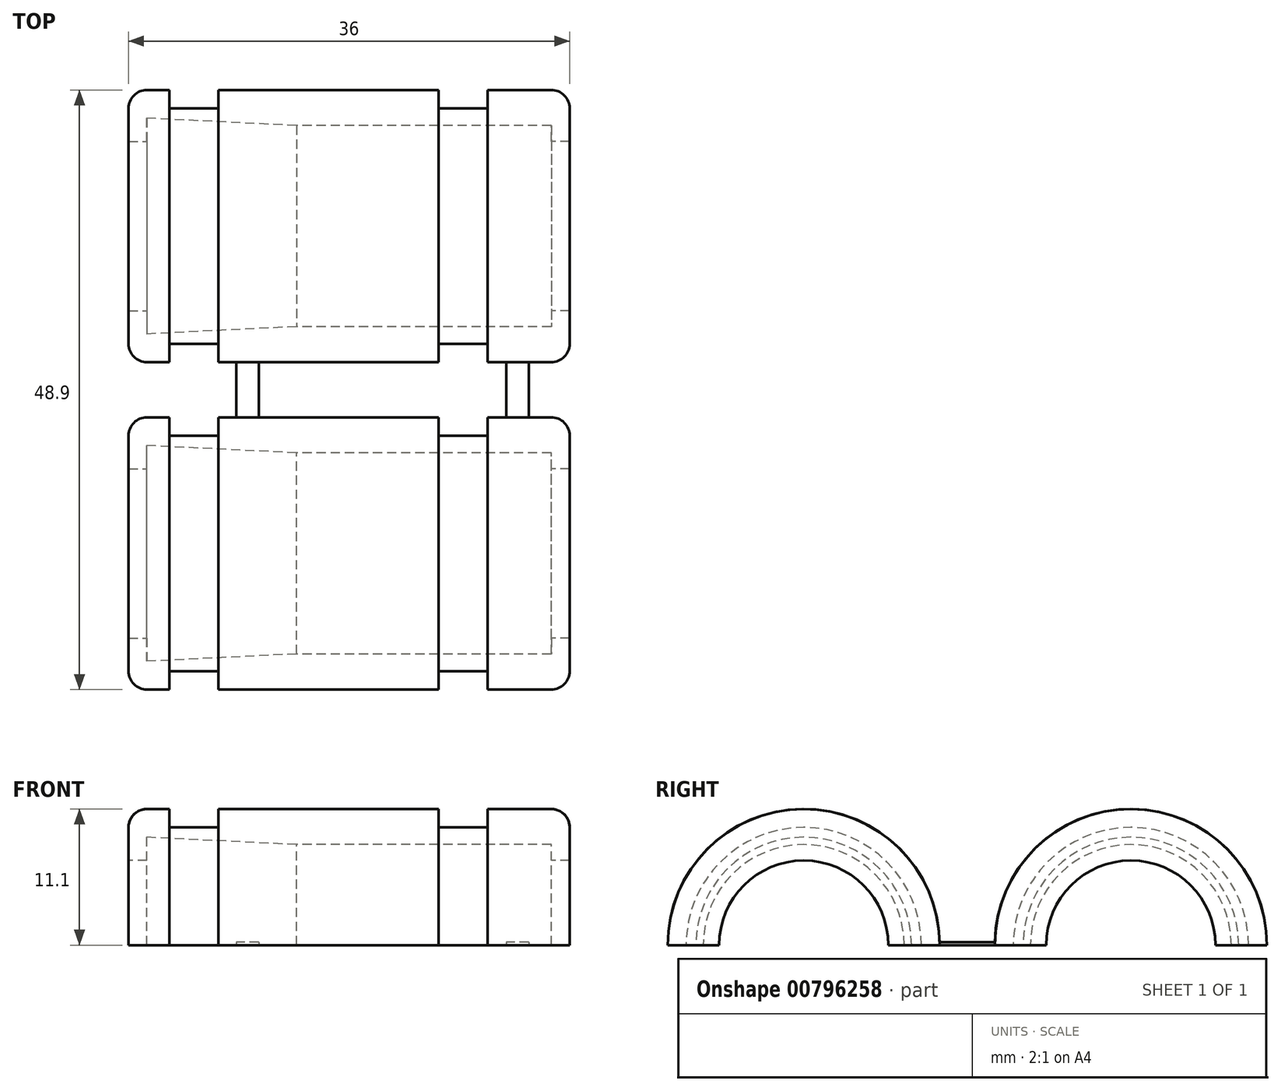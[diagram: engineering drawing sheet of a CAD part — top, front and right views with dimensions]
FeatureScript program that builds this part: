
annotation { "Feature Type Name" : "Feature", "Feature Type Description" : "" }
export const myFeature = defineFeature(function(context is Context, id is Id, definition is map)
    precondition{}
    {
        {
            var Q0;
            Q0=qCreatedBy(makeId("Top.planeOp"),FACE);
            var sketch = newSketch(context, id + "F0", { "sketchPlane" : qUnion([Q0])});
            skLineSegment(sketch, "E0", {"start": v(0, 0) * mm, "end": v(0, 8.8) * mm, "construction": true});
            skLineSegment(sketch, "E1", {"start": v(0, 0) * mm, "end": v(34.5, 0) * mm, "construction": true});
            skLineSegment(sketch, "E2", {"start": v(34.5, 0) * mm, "end": v(34.5, 8.2) * mm, "construction": true});
            skLineSegment(sketch, "E3", {"start": v(12.21, 0) * mm, "end": v(12.21, 8.2) * mm, "construction": true});
            skLineSegment(sketch, "E4", {"start": v(34.5, 0) * mm, "end": v(34.5, 9.6) * mm, "construction": true});
            skLineSegment(sketch, "E5", {"start": v(34.5, 9.6) * mm, "end": v(34.5, 8.2) * mm});
            skLineSegment(sketch, "E6", {"start": v(33, 8.2) * mm, "end": v(12.21, 8.2) * mm});
            skLineSegment(sketch, "E7", {"start": v(12.21, 8.2) * mm, "end": v(0, 8.8) * mm});
            skLineSegment(sketch, "E8.trimOffspring", {"start": v(23.8, 11.1) * mm, "end": v(5.84, 11.1) * mm});
            skLineSegment(sketch, "E9.trimOffspring", {"start": v(1.84, 11.1) * mm, "end": v(0, 11.1) * mm});
            skLineSegment(sketch, "E10", {"start": v(5.84, 11.1) * mm, "end": v(5.84, 9.6) * mm});
            skLineSegment(sketch, "E11", {"start": v(5.84, 9.6) * mm, "end": v(1.84, 9.6) * mm});
            skLineSegment(sketch, "E12", {"start": v(1.84, 9.6) * mm, "end": v(1.84, 11.1) * mm});
            skLineSegment(sketch, "E13", {"start": v(23.8, 11.1) * mm, "end": v(23.8, 9.6) * mm});
            skLineSegment(sketch, "E14", {"start": v(23.8, 9.6) * mm, "end": v(27.8, 9.6) * mm});
            skLineSegment(sketch, "E15", {"start": v(27.8, 9.6) * mm, "end": v(27.8, 11.1) * mm});
            skLineSegment(sketch, "E16", {"start": v(-1.5, 9.6) * mm, "end": v(-1.5, 6.9) * mm});
            skLineSegment(sketch, "E17", {"start": v(-1.5, 6.9) * mm, "end": v(0, 6.9) * mm});
            skLineSegment(sketch, "E18", {"start": v(0, 6.9) * mm, "end": v(0, 8.8) * mm});
            skArc(sketch, "E19.filletArc", {"start": v(34.5, 9.6) * mm, "mid": v(34.06, 10.66) * mm, "end": v(33, 11.1) * mm});
            skArc(sketch, "E20.filletArc", {"start": v(0, 11.1) * mm, "mid": v(-1.06, 10.66) * mm, "end": v(-1.5, 9.6) * mm});
            skLineSegment(sketch, "E21", {"start": v(37.63, 13.35) * mm, "end": v(-4.44, 13.35) * mm, "construction": true});
            skLineSegment(sketch, "E22", {"start": v(23.8, 11.1) * mm, "end": v(23.8, 11.1) * mm});
            skLineSegment(sketch, "E23", {"start": v(27.8, 11.1) * mm, "end": v(33, 11.1) * mm});
            skLineSegment(sketch, "E24", {"start": v(34.5, 8.2) * mm, "end": v(34.5, 6.9) * mm});
            skLineSegment(sketch, "E25", {"start": v(34.5, 6.9) * mm, "end": v(33, 6.9) * mm});
            skLineSegment(sketch, "E26", {"start": v(33, 6.9) * mm, "end": v(33, 8.2) * mm});
            skLineSegment(sketch, "E27.MirrorCS", {"start": v(34.5, 18.5) * mm, "end": v(34.5, 19.8) * mm});
            skLineSegment(sketch, "E28.MirrorCS", {"start": v(34.5, 26.7) * mm, "end": v(34.5, 18.5) * mm, "construction": true});
            skLineSegment(sketch, "E29.MirrorCS", {"start": v(34.5, 17.1) * mm, "end": v(34.5, 18.5) * mm});
            skLineSegment(sketch, "E30.MirrorCS", {"start": v(0, 19.8) * mm, "end": v(0, 17.9) * mm});
            skLineSegment(sketch, "E31.MirrorCS", {"start": v(1.84, 17.1) * mm, "end": v(1.84, 15.6) * mm});
            skLineSegment(sketch, "E32.MirrorCS", {"start": v(33, 18.5) * mm, "end": v(12.21, 18.5) * mm});
            skLineSegment(sketch, "E33.MirrorCS", {"start": v(5.84, 17.1) * mm, "end": v(1.84, 17.1) * mm});
            skLineSegment(sketch, "E34.MirrorCS", {"start": v(-1.5, 17.1) * mm, "end": v(-1.5, 19.8) * mm});
            skLineSegment(sketch, "E35.MirrorCS", {"start": v(1.84, 15.6) * mm, "end": v(0, 15.6) * mm});
            skLineSegment(sketch, "E36.MirrorCS", {"start": v(12.21, 18.5) * mm, "end": v(0, 17.9) * mm});
            skLineSegment(sketch, "E37.MirrorCS", {"start": v(34.5, 19.8) * mm, "end": v(33, 19.8) * mm});
            skLineSegment(sketch, "E38.MirrorCS", {"start": v(33, 19.8) * mm, "end": v(33, 18.5) * mm});
            skLineSegment(sketch, "E39.MirrorCS", {"start": v(0, 26.7) * mm, "end": v(34.5, 26.7) * mm, "construction": true});
            skLineSegment(sketch, "E40.MirrorCS", {"start": v(23.8, 15.6) * mm, "end": v(23.8, 17.1) * mm});
            skLineSegment(sketch, "E41.MirrorCS", {"start": v(23.8, 15.6) * mm, "end": v(5.84, 15.6) * mm});
            skLineSegment(sketch, "E42.MirrorCS", {"start": v(23.8, 17.1) * mm, "end": v(27.8, 17.1) * mm});
            skLineSegment(sketch, "E43.MirrorCS", {"start": v(23.8, 15.6) * mm, "end": v(23.8, 15.6) * mm});
            skLineSegment(sketch, "E44.MirrorCS", {"start": v(27.8, 15.6) * mm, "end": v(33, 15.6) * mm});
            skLineSegment(sketch, "E45.MirrorCS", {"start": v(12.21, 26.7) * mm, "end": v(12.21, 18.5) * mm, "construction": true});
            skLineSegment(sketch, "E46.MirrorCS", {"start": v(27.8, 17.1) * mm, "end": v(27.8, 15.6) * mm});
            skLineSegment(sketch, "E47.MirrorCS", {"start": v(34.5, 26.7) * mm, "end": v(34.5, 17.1) * mm, "construction": true});
            skLineSegment(sketch, "E48.MirrorCS", {"start": v(5.84, 15.6) * mm, "end": v(5.84, 17.1) * mm});
            skLineSegment(sketch, "E49.MirrorCS", {"start": v(-1.5, 19.8) * mm, "end": v(0, 19.8) * mm});
            skLineSegment(sketch, "E50.MirrorCS", {"start": v(0, 26.7) * mm, "end": v(0, 17.9) * mm, "construction": true});
            skArc(sketch, "E51.MirrorCS", {"start": v(0, 15.6) * mm, "mid": v(-1.06, 16.04) * mm, "end": v(-1.5, 17.1) * mm});
            skArc(sketch, "E52.MirrorCS", {"start": v(34.5, 17.1) * mm, "mid": v(34.06, 16.04) * mm, "end": v(33, 15.6) * mm});
            skSolve(sketch);
        }
        {
            var Q0;
            Q0=qCreatedBy(makeId("Top.planeOp"),FACE);
            var sketch = newSketch(context, id + "F1", { "sketchPlane" : qUnion([Q0])});
            skLineSegment(sketch, "E53.bottom", {"start": v(31.16, 10.7) * mm, "end": v(29.33, 10.7) * mm});
            skLineSegment(sketch, "E53.top", {"start": v(31.16, 16.07) * mm, "end": v(29.33, 16.07) * mm});
            skLineSegment(sketch, "E53.left", {"start": v(31.16, 10.7) * mm, "end": v(31.16, 16.07) * mm});
            skLineSegment(sketch, "E53.right", {"start": v(29.33, 10.7) * mm, "end": v(29.33, 16.07) * mm});
            skLineSegment(sketch, "E54.bottom", {"start": v(7.3, 10.7) * mm, "end": v(9.13, 10.7) * mm});
            skLineSegment(sketch, "E54.top", {"start": v(7.3, 16.02) * mm, "end": v(9.13, 16.02) * mm});
            skLineSegment(sketch, "E54.left", {"start": v(7.3, 10.7) * mm, "end": v(7.3, 16.02) * mm});
            skLineSegment(sketch, "E54.right", {"start": v(9.13, 10.7) * mm, "end": v(9.13, 16.02) * mm});
            skSolve(sketch);
        }
        {
            var Q0;
            Q0=makeQuery(id+"F0.imprint","IMPRINT",FACE,{"disambiguationData":[TD([[makeQuery(id+"F0.imprint","IMPRINT",EDGE,{"derivedFrom":sQuery(id+"F0.wireOp",EDGE,"bGX01jQz-EiFG-f5hk-E322-pSOzgLfUBltn")}),1.0]])]});
            var Q1;
            Q1=makeQuery(id+"F0.imprint","IMPRINT",FACE,{"disambiguationData":[TD([[makeQuery(id+"F0.imprint","IMPRINT",EDGE,{"derivedFrom":sQuery(id+"F0.wireOp",EDGE,"E5")}),-1.0]])]});
            var Q2;
            Q2=sQuery(id+"F0.wireOp",EDGE,"E1");
            revolve(context, id + "F2", {"surfaceOperationType" : NewSurfaceOperationType.NEW, "entities" : qUnion([Q0, Q1]), "axis" : qUnion([Q2]), "revolveType" : RevolveType.ONE_DIRECTION, "angle" : 180 * degree});
        }
        {
            var Q0;
            Q0=makeQuery(id+"F0.imprint","IMPRINT",FACE,{"disambiguationData":[TD([[makeQuery(id+"F0.imprint","IMPRINT",EDGE,{"derivedFrom":sQuery(id+"F0.wireOp",EDGE,"E27.MirrorCS")}),1.0]])]});
            var Q1;
            Q1=sQuery(id+"F0.wireOp",EDGE,"E39.MirrorCS");
            revolve(context, id + "F3", {"surfaceOperationType" : NewSurfaceOperationType.NEW, "entities" : qUnion([Q0]), "axis" : qUnion([Q1]), "revolveType" : RevolveType.ONE_DIRECTION, "oppositeDirection" : true, "angle" : 180 * degree});
        }
        {
            var Q0;
            Q0=makeQuery(id+"F1.imprint","IMPRINT",FACE,{"disambiguationData":[TD([[makeQuery(id+"F1.imprint","IMPRINT",EDGE,{"derivedFrom":sQuery(id+"F1.wireOp",EDGE,"E53.bottom")}),-1.0]])]});
            var Q1;
            Q1=makeQuery(id+"F1.imprint","IMPRINT",FACE,{"disambiguationData":[TD([[makeQuery(id+"F1.imprint","IMPRINT",EDGE,{"derivedFrom":sQuery(id+"F1.wireOp",EDGE,"E54.bottom")}),1.0]])]});
            extrude(context, id + "F4", {"entities" : qUnion([Q0, Q1]), "operationType" : NewBodyOperationType.ADD, "depth" : 0.25 * mm, "offsetDistance" : 25 * mm});
        }
    });
